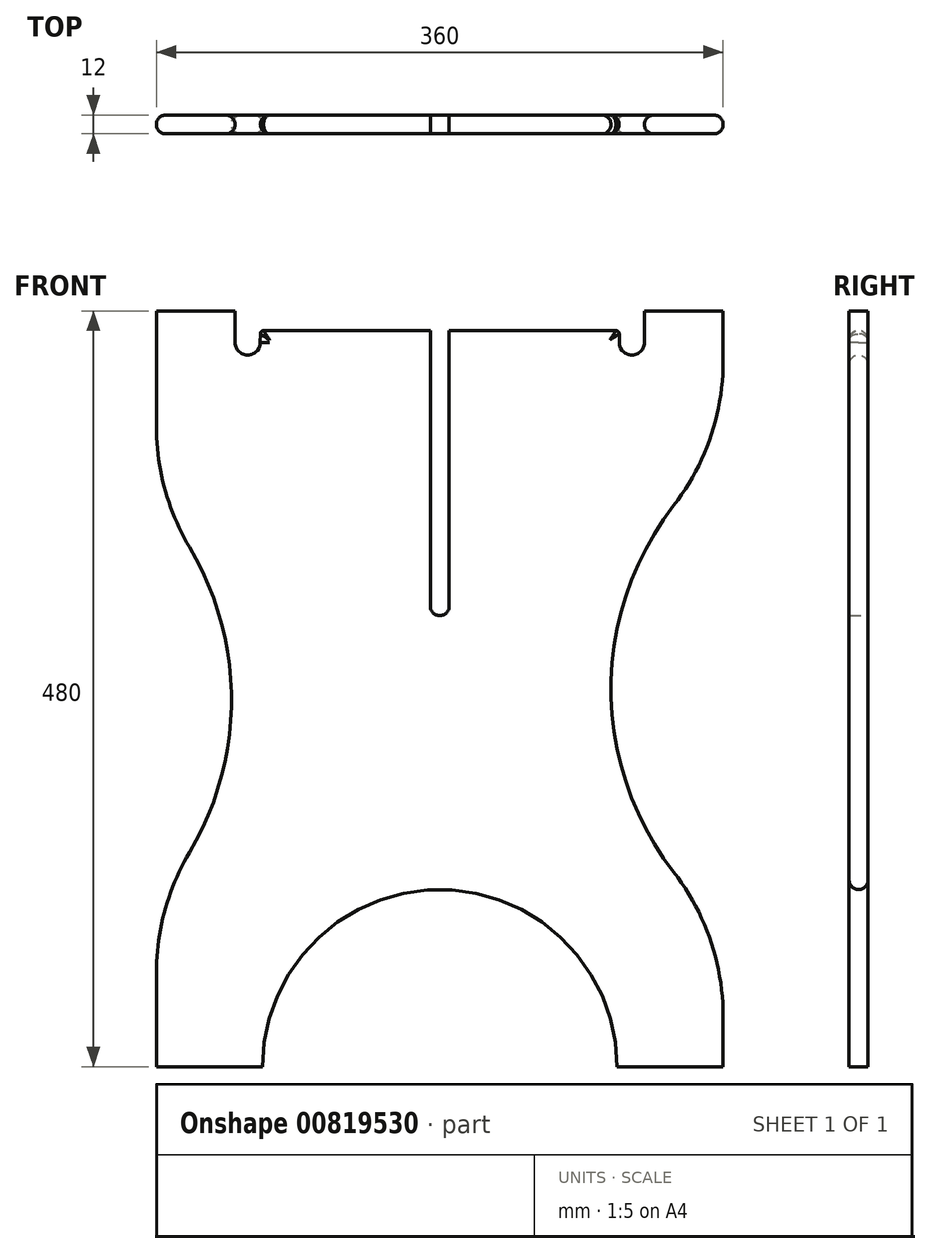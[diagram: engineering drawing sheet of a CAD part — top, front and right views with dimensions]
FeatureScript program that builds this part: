
annotation { "Feature Type Name" : "Feature", "Feature Type Description" : "" }
export const myFeature = defineFeature(function(context is Context, id is Id, definition is map)
    precondition{}
    {
        {
            var Q0;
            Q0=qCreatedBy(makeId("Front.planeOp"),FACE);
            var sketch = newSketch(context, id + "F0", { "sketchPlane" : qUnion([Q0])});
            skLineSegment(sketch, "E0.bottom", {"start": v(-180, -240) * mm, "end": v(-112.5, -240) * mm});
            skLineSegment(sketch, "E0.top", {"start": v(-180, 240) * mm, "end": v(-130, 240) * mm});
            skLineSegment(sketch, "E0.left", {"start": v(-180, -240) * mm, "end": v(-180, -180.56) * mm});
            skLineSegment(sketch, "E0.right", {"start": v(180, -240) * mm, "end": v(180, -208.23) * mm});
            skPoint(sketch, "E0.middle", {"position": v(0, 0) * mm});
            skLineSegment(sketch, "E1.0", {"start": v(-130, 228) * mm, "end": v(-130, 240) * mm});
            skLineSegment(sketch, "E2.0", {"start": v(130, 227.51) * mm, "end": v(130, 240) * mm});
            skLineSegment(sketch, "E3.trimOffspring", {"start": v(130, 240) * mm, "end": v(180, 240) * mm});
            skLineSegment(sketch, "E4.trimOffspring", {"start": v(112.5, -240) * mm, "end": v(180, -240) * mm});
            skArc(sketch, "E5", {"start": v(148.58, 116.36) * mm, "mid": v(108.78, 0) * mm, "end": v(148.58, -116.36) * mm});
            skArc(sketch, "E6", {"start": v(-158.98, -103.98) * mm, "mid": v(-132.35, -6.97) * mm, "end": v(-158.98, 90.04) * mm});
            skLineSegment(sketch, "E7.trimOffspring", {"start": v(-180, 166.62) * mm, "end": v(-180, 240) * mm});
            skLineSegment(sketch, "E8.trimOffspring", {"start": v(180, 208.23) * mm, "end": v(180, 240) * mm});
            skPoint(sketch, "E9.visualSharp", {"position": v(-180, 118.88) * mm});
            skArc(sketch, "E9.filletArc", {"start": v(-180, 166.62) * mm, "mid": v(-174.65, 126.91) * mm, "end": v(-158.98, 90.04) * mm});
            skPoint(sketch, "E10.visualSharp", {"position": v(-180, -132.82) * mm});
            skArc(sketch, "E10.filletArc", {"start": v(-158.98, -103.98) * mm, "mid": v(-174.65, -140.85) * mm, "end": v(-180, -180.56) * mm});
            skPoint(sketch, "E11.visualSharp", {"position": v(180, 148.3) * mm});
            skArc(sketch, "E11.filletArc", {"start": v(148.58, 116.36) * mm, "mid": v(171.93, 159.68) * mm, "end": v(180, 208.23) * mm});
            skPoint(sketch, "E12.visualSharp", {"position": v(180, -148.3) * mm});
            skArc(sketch, "E12.filletArc", {"start": v(180, -208.23) * mm, "mid": v(171.93, -159.68) * mm, "end": v(148.58, -116.36) * mm});
            skArc(sketch, "E13", {"start": v(114, 220) * mm, "mid": v(122, 212) * mm, "end": v(130, 220) * mm});
            skArc(sketch, "E14", {"start": v(-130, 220) * mm, "mid": v(-122, 212) * mm, "end": v(-114, 220) * mm});
            skLineSegment(sketch, "E15", {"start": v(-130, 228) * mm, "end": v(-130, 220) * mm});
            skLineSegment(sketch, "E16", {"start": v(-114, 220) * mm, "end": v(-113.99, 225.5) * mm});
            skLineSegment(sketch, "E17.trimOffspring", {"start": v(-111.99, 227.5) * mm, "end": v(-6, 227.5) * mm});
            skLineSegment(sketch, "E18", {"start": v(130, 227.51) * mm, "end": v(130, 220) * mm});
            skLineSegment(sketch, "E19", {"start": v(114, 220) * mm, "end": v(114, 225.5) * mm});
            skPoint(sketch, "E20.visualSharp", {"position": v(-113.98, 227.5) * mm});
            skArc(sketch, "E20.filletArc", {"start": v(-111.99, 227.5) * mm, "mid": v(-113.4, 226.9) * mm, "end": v(-113.99, 225.5) * mm});
            skPoint(sketch, "E21.visualSharp", {"position": v(114, 227.5) * mm});
            skArc(sketch, "E21.filletArc", {"start": v(114, 225.5) * mm, "mid": v(113.41, 226.92) * mm, "end": v(112, 227.5) * mm});
            skLineSegment(sketch, "E22", {"start": v(-6, 52.5) * mm, "end": v(-6, 227.5) * mm});
            skLineSegment(sketch, "E23", {"start": v(6, 52.5) * mm, "end": v(6, 227.5) * mm});
            skArc(sketch, "E24", {"start": v(-6, 52.5) * mm, "mid": v(0, 46.5) * mm, "end": v(6, 52.5) * mm});
            skPoint(sketch, "E25.center.orphan", {"position": v(0, -240) * mm});
            skArc(sketch, "E26", {"start": v(112.5, -240) * mm, "mid": v(0, -127.5) * mm, "end": v(-112.5, -240) * mm});
            skLineSegment(sketch, "E27.trimOffspring", {"start": v(6, 227.5) * mm, "end": v(112, 227.5) * mm});
            skSolve(sketch);
        }
        {
            var Q0;
            Q0=makeQuery(id+"F0.imprint","IMPRINT",FACE,{"disambiguationData":[TD([[makeQuery(id+"F0.imprint","IMPRINT",EDGE,{"derivedFrom":sQuery(id+"F0.wireOp",EDGE,"E0.bottom")}),1.0]])]});
            extrude(context, id + "F1", {"entities" : qUnion([Q0]), "endBound" : BoundingType.SYMMETRIC, "depth" : 12 * mm, "offsetDistance" : 25 * mm});
        }
        {
            var Q0;
            Q0=makeQuery(id+"F1.opExtrude","CAP_EDGE",EDGE,{"disambiguationData":[OSD([sQuery(id+"F0.wireOp",EDGE,"E0.right")])],"isStart":false});
            var Q1;
            Q1=makeQuery(id+"F1.opExtrude","CAP_EDGE",EDGE,{"disambiguationData":[OSD([sQuery(id+"F0.wireOp",EDGE,"E0.right")])],"isStart":true});
            var Q2;
            Q2=makeQuery(id+"F1.opExtrude","CAP_EDGE",EDGE,{"disambiguationData":[OSD([sQuery(id+"F0.wireOp",EDGE,"E0.left")])],"isStart":false});
            var Q3;
            Q3=makeQuery(id+"F1.opExtrude","CAP_EDGE",EDGE,{"disambiguationData":[OSD([sQuery(id+"F0.wireOp",EDGE,"E0.left")])],"isStart":true});
            var Q4;
            Q4=makeQuery(id+"F1.opExtrude","CAP_EDGE",EDGE,{"disambiguationData":[OSD([sQuery(id+"F0.wireOp",EDGE,"5Ev8Z0yV-7YfI-zG8F-Z9JZ-Wa7wKNcBOxUy")])],"isStart":false});
            var Q5;
            Q5=makeQuery(id+"F1.opExtrude","CAP_EDGE",EDGE,{"disambiguationData":[OSD([sQuery(id+"F0.wireOp",EDGE,"5Ev8Z0yV-7YfI-zG8F-Z9JZ-Wa7wKNcBOxUy")])],"isStart":true});
            var Q6;
            Q6=makeQuery(id+"F1.opExtrude","CAP_EDGE",EDGE,{"disambiguationData":[OSD([sQuery(id+"F0.wireOp",EDGE,"E1.0"),sQuery(id+"F0.wireOp",EDGE,"E15")])],"isStart":false});
            var Q7;
            Q7=makeQuery(id+"F1.opExtrude","CAP_EDGE",EDGE,{"disambiguationData":[OSD([sQuery(id+"F0.wireOp",EDGE,"E1.0"),sQuery(id+"F0.wireOp",EDGE,"E15")])],"isStart":true});
            var Q8;
            Q8=makeQuery(id+"F1.opExtrude","CAP_EDGE",EDGE,{"disambiguationData":[OSD([sQuery(id+"F0.wireOp",EDGE,"E2.0"),sQuery(id+"F0.wireOp",EDGE,"E18")])],"isStart":false});
            var Q9;
            Q9=makeQuery(id+"F1.opExtrude","CAP_EDGE",EDGE,{"disambiguationData":[OSD([sQuery(id+"F0.wireOp",EDGE,"E2.0"),sQuery(id+"F0.wireOp",EDGE,"E18")])],"isStart":true});
            var Q10;
            Q10=makeQuery(id+"F1.opExtrude","CAP_EDGE",EDGE,{"disambiguationData":[OSD([sQuery(id+"F0.wireOp",EDGE,"E17.trimOffspring")])],"isStart":true});
            var Q11;
            Q11=makeQuery(id+"F1.opExtrude","CAP_EDGE",EDGE,{"disambiguationData":[OSD([sQuery(id+"F0.wireOp",EDGE,"E17.trimOffspring")])],"isStart":false});
            fillet(context, id + "F2", {"entities" : qUnion([Q0, Q1, Q2, Q3, Q4, Q5, Q6, Q7, Q8, Q9, Q10, Q11]), "radius" : 6 * mm, "tangentPropagation" : true, "allowEdgeOverflow" : false});
        }
        {
            var Q0;
            Q0=makeQuery(id+"F1.opExtrude","CAP_EDGE",EDGE,{"disambiguationData":[OSD([sQuery(id+"F0.wireOp",EDGE,"E26")])],"isStart":true});
            var Q1;
            Q1=makeQuery(id+"F1.opExtrude","CAP_EDGE",EDGE,{"disambiguationData":[OSD([sQuery(id+"F0.wireOp",EDGE,"E26")])],"isStart":false});
            fillet(context, id + "F3", {"entities" : qUnion([Q0, Q1]), "radius" : 6 * mm, "tangentPropagation" : true, "allowEdgeOverflow" : false});
        }
    });
